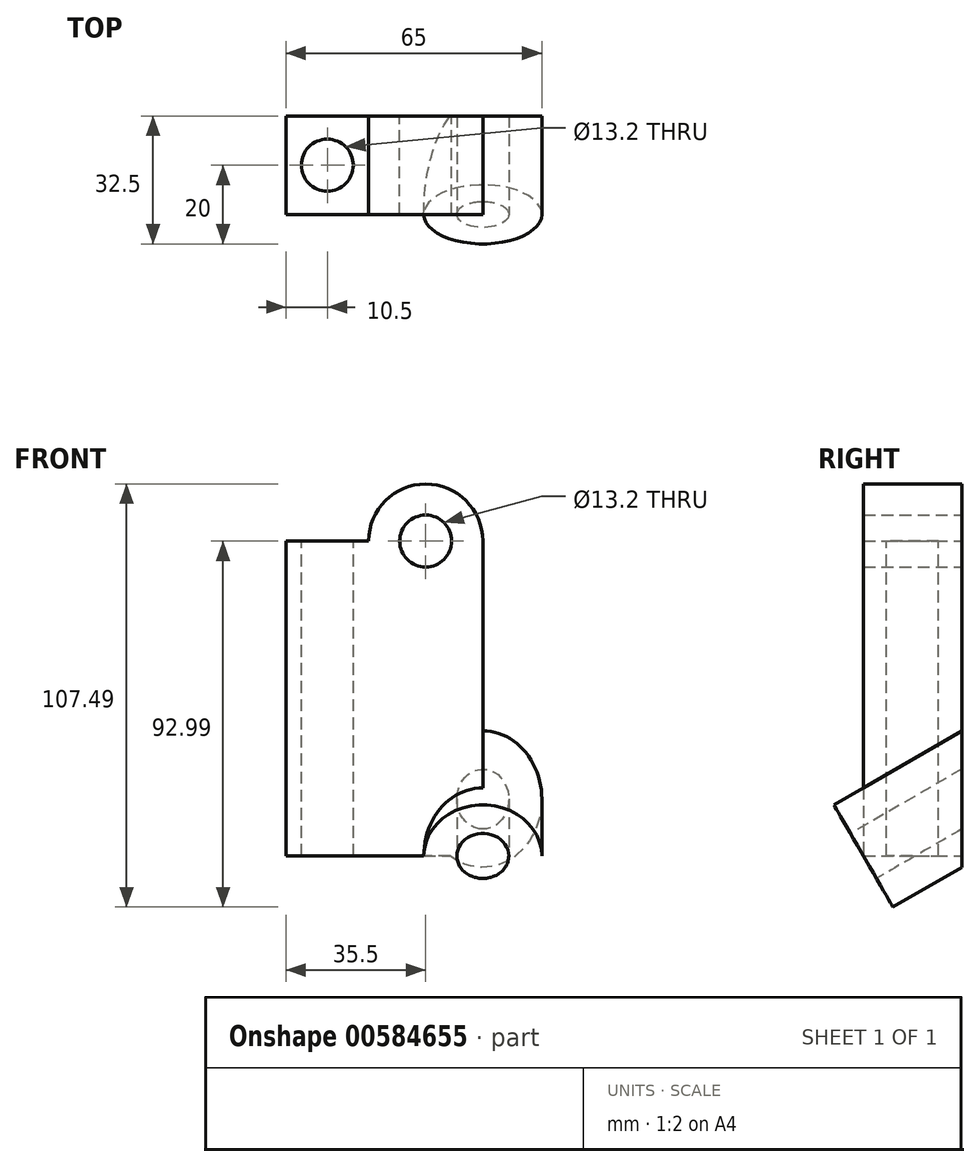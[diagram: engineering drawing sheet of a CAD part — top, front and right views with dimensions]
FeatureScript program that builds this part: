
annotation { "Feature Type Name" : "Feature", "Feature Type Description" : "" }
export const myFeature = defineFeature(function(context is Context, id is Id, definition is map)
    precondition{}
    {
        {
            var Q0;
            Q0=qCreatedBy(makeId("Front.planeOp"),FACE);
            var sketch = newSketch(context, id + "F0", { "sketchPlane" : qUnion([Q0])});
            skLineSegment(sketch, "E0.bottom", {"start": v(25, -40) * mm, "end": v(-25, -40) * mm});
            skLineSegment(sketch, "E0.top", {"start": v(25, 40) * mm, "end": v(-25, 40) * mm});
            skLineSegment(sketch, "E0.left", {"start": v(25, -40) * mm, "end": v(25, 40) * mm});
            skLineSegment(sketch, "E0.right", {"start": v(-25, -40) * mm, "end": v(-25, 40) * mm});
            skPoint(sketch, "E0.middle", {"position": v(0, 0) * mm});
            skCircle(sketch, "E1", {"center": v(10.5, 40) * mm, "radius": 14.5 * mm});
            skSolve(sketch);
        }
        {
            var Q0;
            Q0=qSketchRegion(id+"F0",true);
            extrude(context, id + "F1", {"entities" : qUnion([Q0]), "depth" : 25 * mm, "offsetDistance" : 25 * mm});
        }
        {
            var Q0;
            Q0=makeQuery(id+"F1.opExtrude","CAP_FACE",FACE,{"disambiguationData":[OSD([sQuery(id+"F0.wireOp",EDGE,"E0.bottom"),sQuery(id+"F0.wireOp",EDGE,"E0.top"),sQuery(id+"F0.wireOp",EDGE,"E0.left"),sQuery(id+"F0.wireOp",EDGE,"E0.right"),sQuery(id+"F0.wireOp",EDGE,"E1")])],"isStart":true});
            var sketch = newSketch(context, id + "F2", { "sketchPlane" : qUnion([Q0])});
            skPoint(sketch, "E2", {"position": v(-10.5, 40) * mm});
            skSolve(sketch);
        }
        {
            var Q0;
            Q0=sQuery(id+"F2.wireOp",VERTEX,"E2");
            var Q1;
            Q1=makeQuery(id+"F1.opExtrude","SWEPT_BODY",BODY,{"disambiguationData":[OSD([sQuery(id+"F0.wireOp",EDGE,"E0.bottom"),sQuery(id+"F0.wireOp",EDGE,"E0.top"),sQuery(id+"F0.wireOp",EDGE,"E0.left"),sQuery(id+"F0.wireOp",EDGE,"E0.right"),sQuery(id+"F0.wireOp",EDGE,"E1")])]});
            hole(context, id + "F3", {"style" : HoleStyle.C_BORE, "endStyle" : HoleEndStyle.THROUGH, "holeDiameter" : 13.2 * mm, "cBoreDiameter" : 19.25 * mm, "cBoreDepth" : 0 * mm, "majorDiameter" : 5 * mm, "isTappedThrough" : true, "tappedDepth" : 12 * mm, "tapClearance" : 3, "startFromSketch" : true, "locations" : qUnion([Q0]), "scope" : qUnion([Q1])});
        }
        {
            var Q0;
            Q0=qCreatedBy(makeId("Right.planeOp"),FACE);
            var sketch = newSketch(context, id + "F4", { "sketchPlane" : qUnion([Q0])});
            skLineSegment(sketch, "E3.bottom", {"start": v(-25, 10) * mm, "end": v(-49.3, 10) * mm});
            skLineSegment(sketch, "E3.top", {"start": v(-25, -40) * mm, "end": v(-49.3, -40) * mm});
            skLineSegment(sketch, "E3.left", {"start": v(-25, 10) * mm, "end": v(-25, -40) * mm});
            skLineSegment(sketch, "E3.right", {"start": v(-49.3, 10) * mm, "end": v(-49.3, -40) * mm});
            skSolve(sketch);
        }
        {
            var Q0;
            Q0=qSketchRegion(id+"F4",true);
            extrude(context, id + "F5", {"entities" : qUnion([Q0]), "operationType" : NewBodyOperationType.REMOVE, "oppositeDirection" : true, "depth" : -60 * mm, "offsetDistance" : 25 * mm});
        }
        {
            var Q0;
            Q0=makeQuery(id+"F1.opExtrude","SWEPT_FACE",FACE,{"disambiguationData":[OSD([sQuery(id+"F0.wireOp",EDGE,"E0.top")])]});
            var sketch = newSketch(context, id + "F6", { "sketchPlane" : qUnion([Q0])});
            skPoint(sketch, "E4", {"position": v(-14.5, -12.5) * mm});
            skPoint(sketch, "E4.positionSnap0", {"position": v(-4, -12.5) * mm});
            skSolve(sketch);
        }
        {
            var Q0;
            Q0=sQuery(id+"F6.wireOp",VERTEX,"E4");
            var Q1;
            Q1=makeQuery(id+"F1.opExtrude","SWEPT_BODY",BODY,{"disambiguationData":[OSD([sQuery(id+"F0.wireOp",EDGE,"E0.bottom"),sQuery(id+"F0.wireOp",EDGE,"E0.top"),sQuery(id+"F0.wireOp",EDGE,"E0.left"),sQuery(id+"F0.wireOp",EDGE,"E0.right"),sQuery(id+"F0.wireOp",EDGE,"E1")])]});
            hole(context, id + "F7", {"style" : HoleStyle.C_BORE, "endStyle" : HoleEndStyle.THROUGH, "holeDiameter" : 13.2 * mm, "cBoreDiameter" : 19.25 * mm, "cBoreDepth" : 0 * mm, "majorDiameter" : 5 * mm, "isTappedThrough" : true, "tappedDepth" : 12 * mm, "tapClearance" : 3, "startFromSketch" : true, "locations" : qUnion([Q0]), "scope" : qUnion([Q1])});
        }
        {
            var Q0;
            Q0=makeQuery(id+"F1.opExtrude","CAP_EDGE",EDGE,{"disambiguationData":[OSD([sQuery(id+"F0.wireOp",EDGE,"E0.bottom")])],"isStart":false});
            cPlane(context, id + "F8", {"entities" : qUnion([Q0]), "cplaneType" : CPlaneType.LINE_ANGLE, "offset" : 25 * mm, "angle" : 150 * degree, "width" : 150 * mm, "height" : 150 * mm});
        }
        {
            var Q0;
            Q0=qCreatedBy(id+"F8.planeOp",FACE);
            var sketch = newSketch(context, id + "F9", { "sketchPlane" : qUnion([Q0])});
            skCircle(sketch, "E5", {"center": v(-25, -22.14) * mm, "radius": 15 * mm});
            skSolve(sketch);
        }
        {
            var Q0;
            Q0=makeQuery(id+"F9.imprint","IMPRINT",FACE,{"disambiguationData":[TD([[makeQuery(id+"F9.imprint","IMPRINT",EDGE,{"derivedFrom":sQuery(id+"F9.wireOp",EDGE,"E5")}),1.0]])]});
            extrude(context, id + "F10", {"entities" : qUnion([Q0]), "operationType" : NewBodyOperationType.ADD, "depth" : 52 * mm, "offsetDistance" : 25 * mm});
        }
        {
            var Q0;
            Q0=makeQuery(id+"F10.opExtrude","CAP_FACE",FACE,{"disambiguationData":[OSD([sQuery(id+"F9.wireOp",EDGE,"E5")])],"isStart":true});
            var sketch = newSketch(context, id + "F11", { "sketchPlane" : qUnion([Q0])});
            skPoint(sketch, "E6", {"position": v(25, -22.14) * mm});
            skSolve(sketch);
        }
        {
            var Q0;
            Q0=sQuery(id+"F11.wireOp",VERTEX,"E6");
            var Q1;
            Q1=makeQuery(id+"F1.opExtrude","SWEPT_BODY",BODY,{"disambiguationData":[OSD([sQuery(id+"F0.wireOp",EDGE,"E0.bottom"),sQuery(id+"F0.wireOp",EDGE,"E0.top"),sQuery(id+"F0.wireOp",EDGE,"E0.left"),sQuery(id+"F0.wireOp",EDGE,"E0.right"),sQuery(id+"F0.wireOp",EDGE,"E1")])]});
            hole(context, id + "F12", {"style" : HoleStyle.C_BORE, "endStyle" : HoleEndStyle.THROUGH, "holeDiameter" : 13.2 * mm, "cBoreDiameter" : 19.25 * mm, "cBoreDepth" : 0 * mm, "majorDiameter" : 5 * mm, "isTappedThrough" : true, "tappedDepth" : 12 * mm, "tapClearance" : 3, "startFromSketch" : true, "locations" : qUnion([Q0]), "scope" : qUnion([Q1])});
        }
        {
            var Q0;
            Q0=qCreatedBy(makeId("Right.planeOp"),FACE);
            var sketch = newSketch(context, id + "F13", { "sketchPlane" : qUnion([Q0])});
            skLineSegment(sketch, "E7.bottom", {"start": v(0, 12.88) * mm, "end": v(29.75, 12.88) * mm});
            skLineSegment(sketch, "E7.top", {"start": v(0, -43.67) * mm, "end": v(29.75, -43.67) * mm});
            skLineSegment(sketch, "E7.left", {"start": v(0, 12.88) * mm, "end": v(0, -43.67) * mm});
            skLineSegment(sketch, "E7.right", {"start": v(29.75, 12.88) * mm, "end": v(29.75, -43.67) * mm});
            skSolve(sketch);
        }
        {
            var Q0;
            Q0 = qSketchRegion(id + "F13", true);
            extrude(context, id + "F14", {"entities" : qUnion([Q0]), "operationType" : NewBodyOperationType.REMOVE, "oppositeDirection" : true, "depth" : -50 * mm, "offsetDistance" : 25 * mm});
        }
    });
